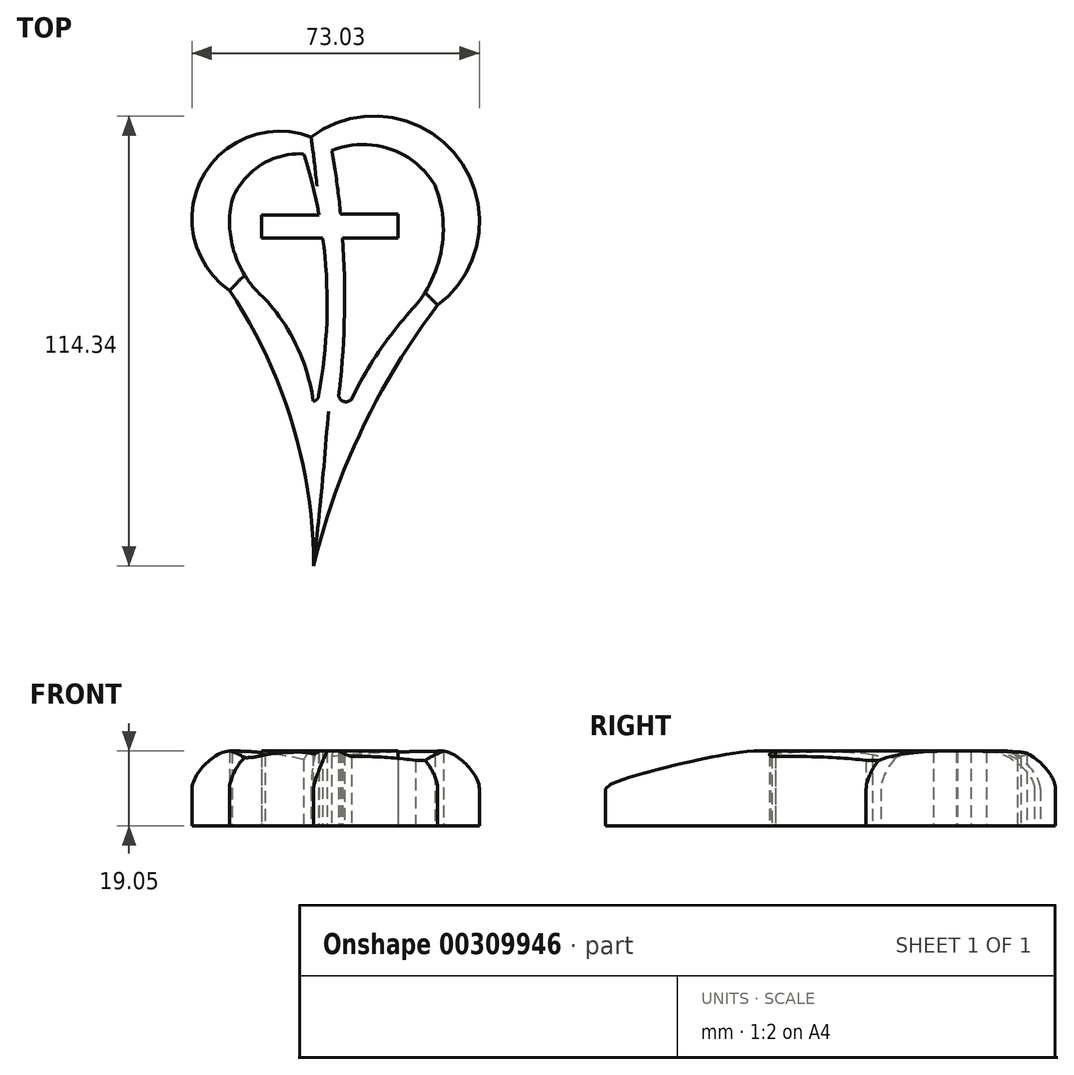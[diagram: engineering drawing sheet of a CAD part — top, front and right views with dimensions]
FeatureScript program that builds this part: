
annotation { "Feature Type Name" : "Feature", "Feature Type Description" : "" }
export const myFeature = defineFeature(function(context is Context, id is Id, definition is map)
    precondition{}
    {
        {
            var Q0;
            Q0=qCreatedBy(makeId("Top.planeOp"),FACE);
            var sketch = newSketch(context, id + "F0", { "sketchPlane" : qUnion([Q0])});
            skArc(sketch, "E0", {"start": v(-25.95, -61.3) * mm, "mid": v(-31.45, -24.72) * mm, "end": v(-47.32, 8.7) * mm});
            skArc(sketch, "E1", {"start": v(0, 4.91) * mm, "mid": v(-9.07, -6.43) * mm, "end": v(-16.34, -19) * mm});
            skArc(sketch, "E2", {"start": v(-24.72, -18.09) * mm, "mid": v(-22.54, 1.92) * mm, "end": v(-23.61, 22.02) * mm});
            skArc(sketch, "E3", {"start": v(-19.58, -18.09) * mm, "mid": v(-18.12, 1.94) * mm, "end": v(-18.56, 22.02) * mm});
            skArc(sketch, "E4", {"start": v(-19.58, -18.09) * mm, "mid": v(-17.72, -19.6) * mm, "end": v(-15.86, -18.09) * mm});
            skArc(sketch, "E5", {"start": v(-26.04, -19.4) * mm, "mid": v(-25.1, -19.02) * mm, "end": v(-24.72, -18.09) * mm});
            skPoint(sketch, "E6.orphan", {"position": v(-25.95, 24.32) * mm});
            skLineSegment(sketch, "E7", {"start": v(-24.54, 27.87) * mm, "end": v(-39.22, 27.87) * mm});
            skLineSegment(sketch, "E8", {"start": v(-39.22, 27.87) * mm, "end": v(-39.22, 22.02) * mm});
            skLineSegment(sketch, "E9", {"start": v(-39.22, 22.02) * mm, "end": v(-23.61, 22.02) * mm});
            skLineSegment(sketch, "E10", {"start": v(-4.43, 22.02) * mm, "end": v(-4.43, 28.16) * mm});
            skLineSegment(sketch, "E11", {"start": v(-4.43, 28.16) * mm, "end": v(-19.58, 28.16) * mm});
            skArc(sketch, "E12.trimOffspring", {"start": v(-24.54, 27.87) * mm, "mid": v(-26.24, 35.69) * mm, "end": v(-28.43, 43.37) * mm});
            skLineSegment(sketch, "E13.trimOffspring", {"start": v(-18.56, 22.02) * mm, "end": v(-4.43, 22.02) * mm});
            skArc(sketch, "E14.trimOffspring", {"start": v(-19.08, 28.16) * mm, "mid": v(-20.04, 36.25) * mm, "end": v(-21.31, 44.29) * mm});
            skPoint(sketch, "E15.start.orphan", {"position": v(5.56, 4.94) * mm});
            skArc(sketch, "E16", {"start": v(5.56, 4.94) * mm, "mid": v(-13.65, -26.54) * mm, "end": v(-25.95, -61.3) * mm});
            skArc(sketch, "E17", {"start": v(-28.43, 43.37) * mm, "mid": v(-39.5, 40.47) * mm, "end": v(-46.68, 31.56) * mm});
            skArc(sketch, "E18", {"start": v(-46.68, 31.56) * mm, "mid": v(-45.93, 17.85) * mm, "end": v(-38.22, 6.48) * mm});
            skPoint(sketch, "E19.end.orphan", {"position": v(-39.75, 4.94) * mm});
            skPoint(sketch, "E19.start.orphan", {"position": v(-26.04, -19.4) * mm});
            skArc(sketch, "E20", {"start": v(-26.04, -19.4) * mm, "mid": v(-30.18, -5.54) * mm, "end": v(-38.22, 6.48) * mm});
            skArc(sketch, "E21", {"start": v(-26.58, 47.7) * mm, "mid": v(-54.23, 37.39) * mm, "end": v(-47.32, 8.7) * mm});
            skArc(sketch, "E22", {"start": v(5.56, 4.94) * mm, "mid": v(10.83, 42.35) * mm, "end": v(-26.58, 47.7) * mm});
            skArc(sketch, "E23", {"start": v(4.88, 35.46) * mm, "mid": v(-6.6, 44.7) * mm, "end": v(-21.31, 44.29) * mm});
            skPoint(sketch, "E24.center.orphan", {"position": v(-15.86, 25.65) * mm});
            skArc(sketch, "E25", {"start": v(0, 4.91) * mm, "mid": v(6.62, 19.52) * mm, "end": v(4.88, 35.46) * mm});
            skLineSegment(sketch, "E26", {"start": v(-56.83, 26.3) * mm, "end": v(-56.83, 27.58) * mm});
            skPoint(sketch, "E27.start.orphan", {"position": v(16.2, 26.3) * mm});
            skPoint(sketch, "E28.start.orphan", {"position": v(-9.21, 53) * mm});
            skSolve(sketch);
        }
        {
            var Q0;
            Q0 = qSketchRegion(id + "F0", true);
            extrude(context, id + "F1", {"entities" : qUnion([Q0]), "depth" : 19.05 * mm});
        }
        {
            var Q0;
            Q0=makeQuery(id+"F1.opExtrude","CAP_EDGE",EDGE,{"disambiguationData":[OSD([sQuery(id+"F0.wireOp",EDGE,"E21")])],"isStart":false});
            var Q1;
            Q1=makeQuery(id+"F1.opExtrude","CAP_EDGE",EDGE,{"disambiguationData":[OSD([sQuery(id+"F0.wireOp",EDGE,"E0")])],"isStart":false});
            var Q2;
            Q2=makeQuery(id+"F1.opExtrude","CAP_EDGE",EDGE,{"disambiguationData":[OSD([sQuery(id+"F0.wireOp",EDGE,"E16")])],"isStart":false});
            var Q3;
            Q3=makeQuery(id+"F1.opExtrude","CAP_EDGE",EDGE,{"disambiguationData":[OSD([sQuery(id+"F0.wireOp",EDGE,"E22")])],"isStart":false});
            fillet(context, id + "F2", {"entities" : qUnion([Q0, Q1, Q2, Q3]), "radius" : 9.65 * mm, "tangentPropagation" : true, "rho" : .3, "crossSection" : FilletCrossSection.CONIC, "allowEdgeOverflow" : false});
        }
    });
